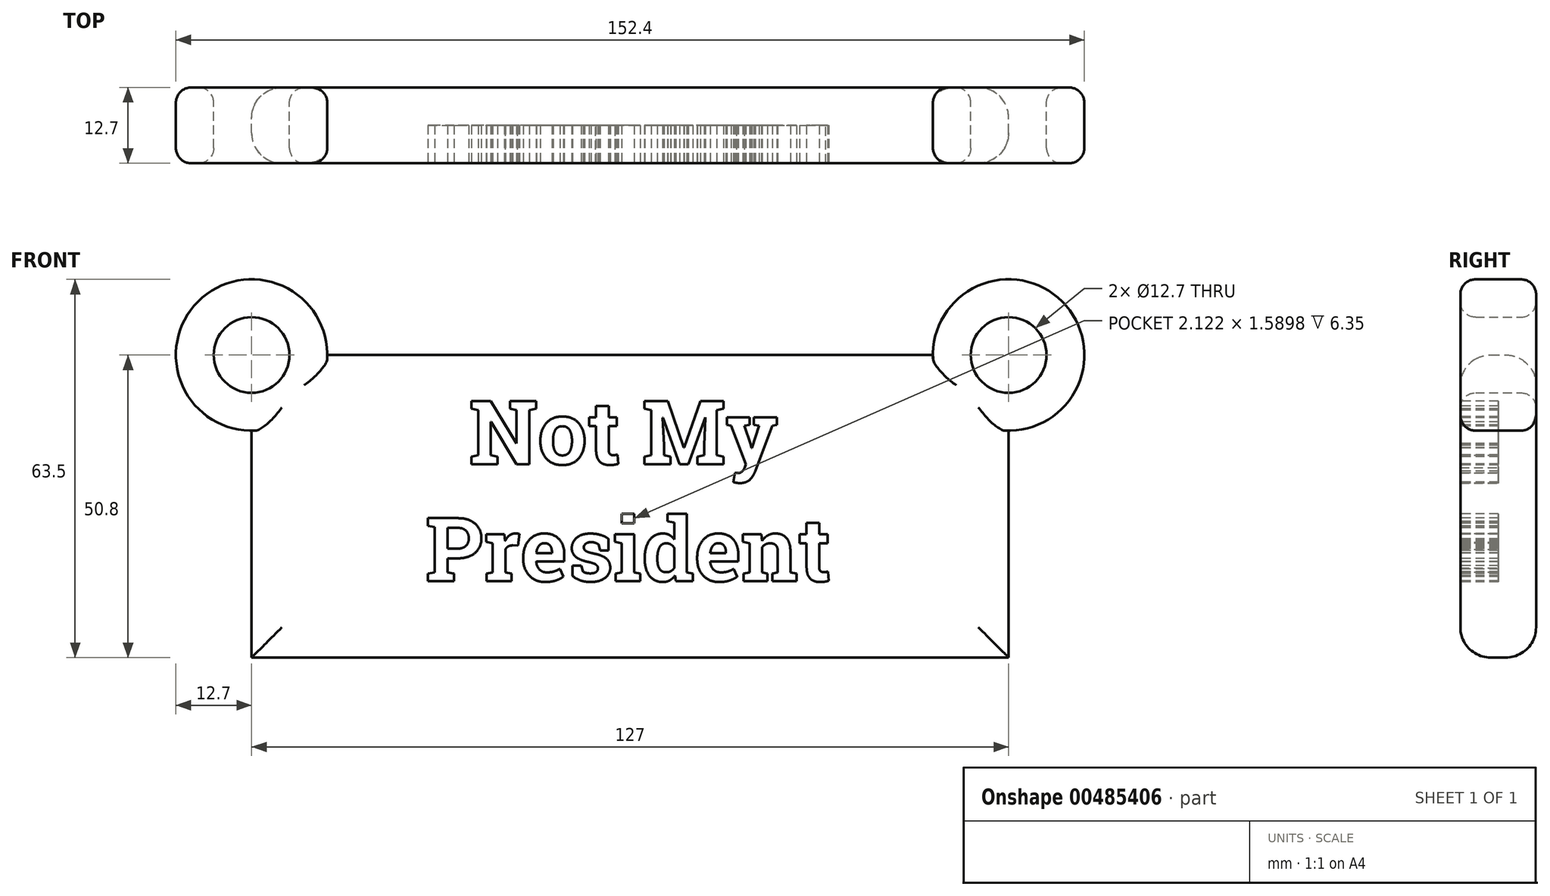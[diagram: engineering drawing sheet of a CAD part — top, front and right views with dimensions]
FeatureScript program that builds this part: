
annotation { "Feature Type Name" : "Feature", "Feature Type Description" : "" }
export const myFeature = defineFeature(function(context is Context, id is Id, definition is map)
    precondition{}
    {
        {
            var Q0;
            Q0=qCreatedBy(makeId("Front.planeOp"),FACE);
            var sketch = newSketch(context, id + "F0", { "sketchPlane" : qUnion([Q0])});
            skLineSegment(sketch, "E0.bottom", {"start": v(-127, 50.8) * mm, "end": v(0, 50.8) * mm});
            skLineSegment(sketch, "E0.top", {"start": v(-127, 0) * mm, "end": v(0, 0) * mm});
            skLineSegment(sketch, "E0.left", {"start": v(-127, 50.8) * mm, "end": v(-127, 0) * mm});
            skLineSegment(sketch, "E0.right", {"start": v(0, 50.8) * mm, "end": v(0, 0) * mm});
            skCircle(sketch, "E1", {"center": v(-127, 50.8) * mm, "radius": 6.35 * mm});
            skCircle(sketch, "E2", {"center": v(0, 50.8) * mm, "radius": 12.7 * mm});
            skCircle(sketch, "E3", {"center": v(0, 50.8) * mm, "radius": 6.35 * mm});
            skCircle(sketch, "E4", {"center": v(-127, 50.8) * mm, "radius": 12.7 * mm});
            skSolve(sketch);
        }
        {
            var Q0;
            Q0=qSketchRegion(id+"F0",true);
            extrude(context, id + "F1", {"entities" : qUnion([Q0]), "depth" : 12.7 * mm});
        }
        {
            var Q0;
            Q0=makeQuery(id+"F1.opExtrude","CAP_FACE",FACE,{"disambiguationData":[OSD([sQuery(id+"F0.wireOp",EDGE,"E0.bottom"),sQuery(id+"F0.wireOp",EDGE,"E0.top"),sQuery(id+"F0.wireOp",EDGE,"E0.left"),sQuery(id+"F0.wireOp",EDGE,"E0.right"),sQuery(id+"F0.wireOp",EDGE,"E1"),sQuery(id+"F0.wireOp",EDGE,"E2"),sQuery(id+"F0.wireOp",EDGE,"E3"),sQuery(id+"F0.wireOp",EDGE,"E4")])],"isStart":false});
            var sketch = newSketch(context, id + "F2", { "sketchPlane" : qUnion([Q0])});
            skText(sketch, "E5", { "text": "  Not My\nPresident", "fontName": "RobotoSlab-Bold.ttf"});
            const initialGuessF2  = {"E5": [-0.0978, 0.03247, 1, 0, 0.01071]};
            skSetInitialGuess(sketch, initialGuessF2);
            skSolve(sketch);
        }
        {
            var Q0;
            Q0=qSketchRegion(id+"F2",true);
            extrude(context, id + "F3", {"entities" : qUnion([Q0]), "operationType" : NewBodyOperationType.REMOVE, "oppositeDirection" : true, "depth" : 6.35 * mm});
        }
        {
            var Q0;
            Q0=makeQuery(id+"F1.opExtrude","CAP_EDGE",EDGE,{"disambiguationData":[OSD([sQuery(id+"F0.wireOp",EDGE,"E1")])],"isStart":false});
            var Q1;
            Q1=makeQuery(id+"F1.opExtrude","CAP_EDGE",EDGE,{"disambiguationData":[OSD([sQuery(id+"F0.wireOp",EDGE,"E3")])],"isStart":false});
            var Q2;
            Q2=makeQuery(id+"F1.opExtrude","CAP_EDGE",EDGE,{"disambiguationData":[OSD([sQuery(id+"F0.wireOp",EDGE,"E1")])],"isStart":true});
            var Q3;
            Q3=makeQuery(id+"F1.opExtrude","CAP_EDGE",EDGE,{"disambiguationData":[OSD([sQuery(id+"F0.wireOp",EDGE,"E3")])],"isStart":true});
            var Q4;
            Q4=makeQuery(id+"F1.opExtrude","CAP_EDGE",EDGE,{"disambiguationData":[OSD([sQuery(id+"F0.wireOp",EDGE,"E4")])],"isStart":false});
            var Q5;
            Q5=makeQuery(id+"F1.opExtrude","CAP_EDGE",EDGE,{"disambiguationData":[OSD([sQuery(id+"F0.wireOp",EDGE,"E4")])],"isStart":true});
            var Q6;
            Q6=makeQuery(id+"F1.opExtrude","CAP_EDGE",EDGE,{"disambiguationData":[OSD([sQuery(id+"F0.wireOp",EDGE,"E2")])],"isStart":true});
            var Q7;
            Q7=makeQuery(id+"F1.opExtrude","CAP_EDGE",EDGE,{"disambiguationData":[OSD([sQuery(id+"F0.wireOp",EDGE,"E2")])],"isStart":false});
            fillet(context, id + "F4", {"entities" : qUnion([Q0, Q1, Q2, Q3, Q4, Q5, Q6, Q7]), "radius" : 2.54 * mm, "tangentPropagation" : true, "allowEdgeOverflow" : false});
        }
        {
            var Q0;
            Q0=makeQuery(id+"F1.opExtrude","CAP_EDGE",EDGE,{"disambiguationData":[OSD([sQuery(id+"F0.wireOp",EDGE,"E0.bottom")])],"isStart":false});
            var Q1;
            Q1=makeQuery(id+"F1.opExtrude","CAP_EDGE",EDGE,{"disambiguationData":[OSD([sQuery(id+"F0.wireOp",EDGE,"E0.bottom")])],"isStart":true});
            var Q2;
            Q2=makeQuery(id+"F1.opExtrude","CAP_EDGE",EDGE,{"disambiguationData":[OSD([sQuery(id+"F0.wireOp",EDGE,"E0.right")])],"isStart":false});
            var Q3;
            Q3=makeQuery(id+"F1.opExtrude","CAP_EDGE",EDGE,{"disambiguationData":[OSD([sQuery(id+"F0.wireOp",EDGE,"E0.right")])],"isStart":true});
            var Q4;
            Q4=makeQuery(id+"F1.opExtrude","CAP_EDGE",EDGE,{"disambiguationData":[OSD([sQuery(id+"F0.wireOp",EDGE,"E0.top")])],"isStart":false});
            var Q5;
            Q5=makeQuery(id+"F1.opExtrude","CAP_EDGE",EDGE,{"disambiguationData":[OSD([sQuery(id+"F0.wireOp",EDGE,"E0.left")])],"isStart":false});
            var Q6;
            Q6=makeQuery(id+"F1.opExtrude","CAP_EDGE",EDGE,{"disambiguationData":[OSD([sQuery(id+"F0.wireOp",EDGE,"E0.top")])],"isStart":true});
            var Q7;
            Q7=makeQuery(id+"F1.opExtrude","CAP_EDGE",EDGE,{"disambiguationData":[OSD([sQuery(id+"F0.wireOp",EDGE,"E0.left")])],"isStart":true});
            fillet(context, id + "F5", {"entities" : qUnion([Q0, Q1, Q2, Q3, Q4, Q5, Q6, Q7]), "radius" : 5.08 * mm, "tangentPropagation" : true, "allowEdgeOverflow" : false});
        }
    });
